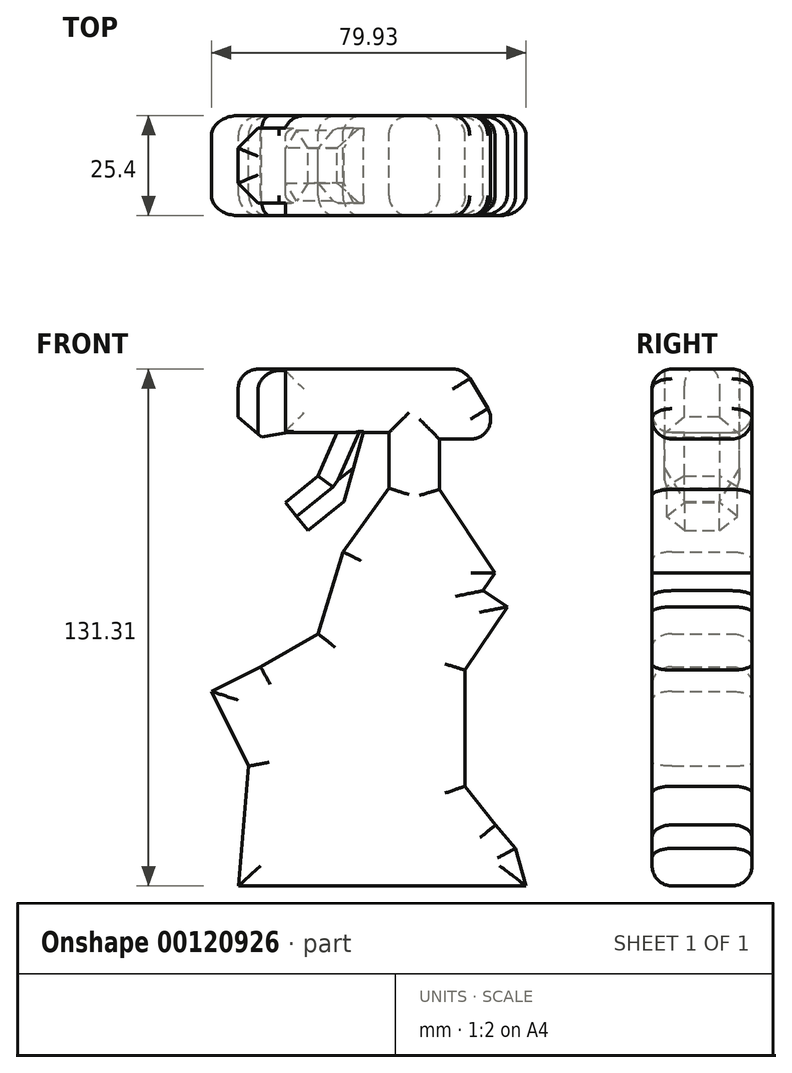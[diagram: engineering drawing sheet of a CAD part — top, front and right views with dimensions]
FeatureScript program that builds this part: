
annotation { "Feature Type Name" : "Feature", "Feature Type Description" : "" }
export const myFeature = defineFeature(function(context is Context, id is Id, definition is map)
    precondition{}
    {
        {
            var Q0;
            Q0=qCreatedBy(makeId("Front.planeOp"),FACE);
            var sketch = newSketch(context, id + "F0", { "sketchPlane" : qUnion([Q0])});
            skLineSegment(sketch, "E0", {"start": v(-38.14, -37.7) * mm, "end": v(34.86, -37.7) * mm});
            skLineSegment(sketch, "E1", {"start": v(34.86, -37.7) * mm, "end": v(32.18, -28.16) * mm});
            skLineSegment(sketch, "E2", {"start": v(32.18, -28.16) * mm, "end": v(27.12, -22.2) * mm});
            skLineSegment(sketch, "E3", {"start": v(27.12, -22.2) * mm, "end": v(19.37, -12.37) * mm});
            skLineSegment(sketch, "E4", {"start": v(19.37, -12.37) * mm, "end": v(19.37, 17.13) * mm});
            skLineSegment(sketch, "E5", {"start": v(19.37, 17.13) * mm, "end": v(30.1, 33.23) * mm});
            skLineSegment(sketch, "E6", {"start": v(30.1, 33.23) * mm, "end": v(23.98, 37.3) * mm});
            skLineSegment(sketch, "E7", {"start": v(23.98, 37.3) * mm, "end": v(26.96, 41.78) * mm});
            skLineSegment(sketch, "E8", {"start": v(26.96, 41.78) * mm, "end": v(12.81, 63.02) * mm});
            skLineSegment(sketch, "E9", {"start": v(12.81, 63.02) * mm, "end": v(12.81, 75.84) * mm});
            skLineSegment(sketch, "E10", {"start": v(12.81, 75.84) * mm, "end": v(29.8, 75.84) * mm});
            skLineSegment(sketch, "E11", {"start": v(29.8, 75.84) * mm, "end": v(19.07, 93.6) * mm});
            skLineSegment(sketch, "E12", {"start": v(19.07, 93.6) * mm, "end": v(-15.87, 93.6) * mm});
            skLineSegment(sketch, "E13", {"start": v(-15.87, 93.6) * mm, "end": v(-26.3, 93.6) * mm});
            skLineSegment(sketch, "E14", {"start": v(-26.3, 93.6) * mm, "end": v(-26.3, 77.44) * mm});
            skLineSegment(sketch, "E15", {"start": v(-26.3, 77.44) * mm, "end": v(0, 77.44) * mm});
            skLineSegment(sketch, "E16", {"start": v(0, 77.44) * mm, "end": v(0, 63.36) * mm});
            skLineSegment(sketch, "E17", {"start": v(0, 63.36) * mm, "end": v(-11.7, 47.2) * mm});
            skLineSegment(sketch, "E18", {"start": v(-11.7, 47.2) * mm, "end": v(-17.95, 26.33) * mm});
            skLineSegment(sketch, "E19", {"start": v(-17.95, 26.33) * mm, "end": v(-32.56, 18) * mm});
            skLineSegment(sketch, "E20", {"start": v(-32.56, 18) * mm, "end": v(-45.07, 11.73) * mm});
            skLineSegment(sketch, "E21", {"start": v(-45.07, 11.73) * mm, "end": v(-35.58, -7.25) * mm});
            skLineSegment(sketch, "E22", {"start": v(-35.58, -7.25) * mm, "end": v(-38.14, -37.7) * mm});
            skLineSegment(sketch, "E23", {"start": v(-26.3, 93.6) * mm, "end": v(-38.3, 93.6) * mm});
            skLineSegment(sketch, "E24", {"start": v(-38.3, 93.6) * mm, "end": v(-38.3, 75.35) * mm});
            skLineSegment(sketch, "E25", {"start": v(-38.3, 75.35) * mm, "end": v(-26.3, 77.44) * mm});
            skLineSegment(sketch, "E26", {"start": v(-13.15, 77.44) * mm, "end": v(-17.95, 66.49) * mm});
            skLineSegment(sketch, "E27", {"start": v(-17.95, 66.49) * mm, "end": v(-26.3, 59.7) * mm});
            skLineSegment(sketch, "E28", {"start": v(-26.3, 59.7) * mm, "end": v(-20.54, 52.62) * mm});
            skLineSegment(sketch, "E29", {"start": v(-20.54, 52.62) * mm, "end": v(-11.43, 60.02) * mm});
            skLineSegment(sketch, "E30", {"start": v(-11.43, 60.02) * mm, "end": v(-6.48, 77.44) * mm});
            skSolve(sketch);
        }
        {
            var Q0;
            Q0=makeQuery(id+"F0.imprint","IMPRINT",FACE,{"disambiguationData":[TD([[makeQuery(id+"F0.imprint","IMPRINT",EDGE,{"derivedFrom":sQuery(id+"F0.wireOp",EDGE,"E0")}),1.0]])]});
            extrude(context, id + "F1", {"entities" : qUnion([Q0]), "endBound" : BoundingType.SYMMETRIC, "depth" : 25.4 * mm});
        }
        {
            var Q0;
            Q0=makeQuery(id+"F0.imprint","IMPRINT",FACE,{"disambiguationData":[TD([[makeQuery(id+"F0.imprint","IMPRINT",EDGE,{"derivedFrom":sQuery(id+"F0.wireOp",EDGE,"E14")}),-1.0]])]});
            var Q1;
            {var subQ0=sQuery(id+"F0.wireOp",EDGE,"E26");Q1=makeQuery(id+"F0.imprint","IMPRINT",FACE,{"disambiguationData":[TD([[makeQuery(id+"F0.imprint","IMPRINT",EDGE,{"derivedFrom":subQ0}),1.0]])]});}
            extrude(context, id + "F2", {"entities" : qUnion([Q0, Q1]), "operationType" : NewBodyOperationType.ADD, "endBound" : BoundingType.SYMMETRIC, "depth" : 19.05 * mm});
        }
        {
            var Q0;
            Q0=makeQuery(id+"F1.opExtrude","CAP_EDGE",EDGE,{"disambiguationData":[OSD([sQuery(id+"F0.wireOp",EDGE,"E22")])],"isStart":false});
            var Q1;
            Q1=makeQuery(id+"F1.opExtrude","CAP_EDGE",EDGE,{"disambiguationData":[OSD([sQuery(id+"F0.wireOp",EDGE,"E21")])],"isStart":false});
            var Q2;
            Q2=makeQuery(id+"F1.opExtrude","CAP_EDGE",EDGE,{"disambiguationData":[OSD([sQuery(id+"F0.wireOp",EDGE,"E0")])],"isStart":false});
            var Q3;
            Q3=makeQuery(id+"F1.opExtrude","CAP_EDGE",EDGE,{"disambiguationData":[OSD([sQuery(id+"F0.wireOp",EDGE,"E1")])],"isStart":false});
            var Q4;
            Q4=makeQuery(id+"F1.opExtrude","CAP_EDGE",EDGE,{"disambiguationData":[OSD([sQuery(id+"F0.wireOp",EDGE,"E20")])],"isStart":false});
            var Q5;
            Q5=makeQuery(id+"F1.opExtrude","CAP_EDGE",EDGE,{"disambiguationData":[OSD([sQuery(id+"F0.wireOp",EDGE,"E18")])],"isStart":false});
            var Q6;
            Q6=makeQuery(id+"F1.opExtrude","CAP_EDGE",EDGE,{"disambiguationData":[OSD([sQuery(id+"F0.wireOp",EDGE,"E17")])],"isStart":false});
            var Q7;
            Q7=makeQuery(id+"F1.opExtrude","CAP_EDGE",EDGE,{"disambiguationData":[OSD([sQuery(id+"F0.wireOp",EDGE,"E16")])],"isStart":false});
            var Q8;
            Q8=makeQuery(id+"F1.opExtrude","CAP_EDGE",EDGE,{"disambiguationData":[OSD([sQuery(id+"F0.wireOp",EDGE,"E15")])],"isStart":false});
            var Q9;
            Q9=makeQuery(id+"F1.opExtrude","CAP_EDGE",EDGE,{"disambiguationData":[OSD([sQuery(id+"F0.wireOp",EDGE,"E12"),sQuery(id+"F0.wireOp",EDGE,"E13")])],"isStart":false});
            var Q10;
            Q10=makeQuery(id+"F1.opExtrude","CAP_EDGE",EDGE,{"disambiguationData":[OSD([sQuery(id+"F0.wireOp",EDGE,"E11")])],"isStart":false});
            var Q11;
            Q11=makeQuery(id+"F1.opExtrude","CAP_EDGE",EDGE,{"disambiguationData":[OSD([sQuery(id+"F0.wireOp",EDGE,"E10")])],"isStart":false});
            var Q12;
            Q12=makeQuery(id+"F1.opExtrude","CAP_EDGE",EDGE,{"disambiguationData":[OSD([sQuery(id+"F0.wireOp",EDGE,"E9")])],"isStart":false});
            var Q13;
            Q13=makeQuery(id+"F1.opExtrude","CAP_EDGE",EDGE,{"disambiguationData":[OSD([sQuery(id+"F0.wireOp",EDGE,"E8")])],"isStart":false});
            var Q14;
            Q14=makeQuery(id+"F1.opExtrude","CAP_EDGE",EDGE,{"disambiguationData":[OSD([sQuery(id+"F0.wireOp",EDGE,"E7")])],"isStart":false});
            var Q15;
            Q15=makeQuery(id+"F1.opExtrude","CAP_EDGE",EDGE,{"disambiguationData":[OSD([sQuery(id+"F0.wireOp",EDGE,"E6")])],"isStart":false});
            var Q16;
            Q16=makeQuery(id+"F1.opExtrude","CAP_EDGE",EDGE,{"disambiguationData":[OSD([sQuery(id+"F0.wireOp",EDGE,"E5")])],"isStart":false});
            var Q17;
            Q17=makeQuery(id+"F1.opExtrude","CAP_EDGE",EDGE,{"disambiguationData":[OSD([sQuery(id+"F0.wireOp",EDGE,"E4")])],"isStart":false});
            var Q18;
            Q18=makeQuery(id+"F1.opExtrude","CAP_EDGE",EDGE,{"disambiguationData":[OSD([sQuery(id+"F0.wireOp",EDGE,"E3")])],"isStart":false});
            var Q19;
            Q19=makeQuery(id+"F1.opExtrude","CAP_EDGE",EDGE,{"disambiguationData":[OSD([sQuery(id+"F0.wireOp",EDGE,"E2")])],"isStart":false});
            var Q20;
            Q20=makeQuery(id+"F1.opExtrude","CAP_EDGE",EDGE,{"disambiguationData":[OSD([sQuery(id+"F0.wireOp",EDGE,"E11")])],"isStart":true});
            var Q21;
            Q21=makeQuery(id+"F1.opExtrude","CAP_EDGE",EDGE,{"disambiguationData":[OSD([sQuery(id+"F0.wireOp",EDGE,"E12"),sQuery(id+"F0.wireOp",EDGE,"E13")])],"isStart":true});
            var Q22;
            Q22=makeQuery(id+"F1.opExtrude","CAP_EDGE",EDGE,{"disambiguationData":[OSD([sQuery(id+"F0.wireOp",EDGE,"E14")])],"isStart":true});
            var Q23;
            Q23=makeQuery(id+"F1.opExtrude","CAP_EDGE",EDGE,{"disambiguationData":[OSD([sQuery(id+"F0.wireOp",EDGE,"E19")])],"isStart":false});
            fillet(context, id + "F3", {"entities" : qUnion([Q0, Q1, Q2, Q3, Q4, Q5, Q6, Q7, Q8, Q9, Q10, Q11, Q12, Q13, Q14, Q15, Q16, Q17, Q18, Q19, Q20, Q21, Q22, Q23]), "radius" : 5.08 * mm, "tangentPropagation" : true, "allowEdgeOverflow" : false});
        }
        {
            var Q0;
            Q0=makeQuery(id+"F1.opExtrude","CAP_EDGE",EDGE,{"disambiguationData":[OSD([sQuery(id+"F0.wireOp",EDGE,"E9")])],"isStart":true});
            var Q1;
            Q1=makeQuery(id+"F1.opExtrude","CAP_EDGE",EDGE,{"disambiguationData":[OSD([sQuery(id+"F0.wireOp",EDGE,"E10")])],"isStart":true});
            var Q2;
            Q2=makeQuery(id+"F1.opExtrude","CAP_EDGE",EDGE,{"disambiguationData":[OSD([sQuery(id+"F0.wireOp",EDGE,"E8")])],"isStart":true});
            var Q3;
            Q3=makeQuery(id+"F1.opExtrude","CAP_EDGE",EDGE,{"disambiguationData":[OSD([sQuery(id+"F0.wireOp",EDGE,"E7")])],"isStart":true});
            var Q4;
            Q4=makeQuery(id+"F1.opExtrude","CAP_EDGE",EDGE,{"disambiguationData":[OSD([sQuery(id+"F0.wireOp",EDGE,"E6")])],"isStart":true});
            var Q5;
            Q5=makeQuery(id+"F1.opExtrude","CAP_EDGE",EDGE,{"disambiguationData":[OSD([sQuery(id+"F0.wireOp",EDGE,"E4")])],"isStart":true});
            var Q6;
            Q6=makeQuery(id+"F1.opExtrude","CAP_EDGE",EDGE,{"disambiguationData":[OSD([sQuery(id+"F0.wireOp",EDGE,"E5")])],"isStart":true});
            var Q7;
            Q7=makeQuery(id+"F1.opExtrude","CAP_EDGE",EDGE,{"disambiguationData":[OSD([sQuery(id+"F0.wireOp",EDGE,"E3")])],"isStart":true});
            var Q8;
            Q8=makeQuery(id+"F1.opExtrude","CAP_EDGE",EDGE,{"disambiguationData":[OSD([sQuery(id+"F0.wireOp",EDGE,"E2")])],"isStart":true});
            var Q9;
            Q9=makeQuery(id+"F1.opExtrude","CAP_EDGE",EDGE,{"disambiguationData":[OSD([sQuery(id+"F0.wireOp",EDGE,"E0")])],"isStart":true});
            var Q10;
            Q10=makeQuery(id+"F1.opExtrude","CAP_EDGE",EDGE,{"disambiguationData":[OSD([sQuery(id+"F0.wireOp",EDGE,"E22")])],"isStart":true});
            var Q11;
            Q11=makeQuery(id+"F1.opExtrude","CAP_EDGE",EDGE,{"disambiguationData":[OSD([sQuery(id+"F0.wireOp",EDGE,"E1")])],"isStart":true});
            var Q12;
            Q12=makeQuery(id+"F1.opExtrude","CAP_EDGE",EDGE,{"disambiguationData":[OSD([sQuery(id+"F0.wireOp",EDGE,"E21")])],"isStart":true});
            var Q13;
            Q13=makeQuery(id+"F1.opExtrude","CAP_EDGE",EDGE,{"disambiguationData":[OSD([sQuery(id+"F0.wireOp",EDGE,"E20")])],"isStart":true});
            var Q14;
            Q14=makeQuery(id+"F1.opExtrude","CAP_EDGE",EDGE,{"disambiguationData":[OSD([sQuery(id+"F0.wireOp",EDGE,"E19")])],"isStart":true});
            var Q15;
            Q15=makeQuery(id+"F1.opExtrude","CAP_EDGE",EDGE,{"disambiguationData":[OSD([sQuery(id+"F0.wireOp",EDGE,"E18")])],"isStart":true});
            var Q16;
            Q16=makeQuery(id+"F1.opExtrude","CAP_EDGE",EDGE,{"disambiguationData":[OSD([sQuery(id+"F0.wireOp",EDGE,"E17")])],"isStart":true});
            var Q17;
            Q17=makeQuery(id+"F1.opExtrude","CAP_EDGE",EDGE,{"disambiguationData":[OSD([sQuery(id+"F0.wireOp",EDGE,"E16")])],"isStart":true});
            var Q18;
            Q18=makeQuery(id+"F1.opExtrude","CAP_EDGE",EDGE,{"disambiguationData":[OSD([sQuery(id+"F0.wireOp",EDGE,"E15")])],"isStart":true});
            fillet(context, id + "F4", {"entities" : qUnion([Q0, Q1, Q2, Q3, Q4, Q5, Q6, Q7, Q8, Q9, Q10, Q11, Q12, Q13, Q14, Q15, Q16, Q17, Q18]), "radius" : 5.08 * mm, "tangentPropagation" : true, "allowEdgeOverflow" : false});
        }
        {
            var Q0;
            Q0=makeQuery(id+"F2.opExtrude","CAP_EDGE",EDGE,{"disambiguationData":[OSD([sQuery(id+"F0.wireOp",EDGE,"E27")])],"isStart":true});
            var Q1;
            Q1=makeQuery(id+"F2.opExtrude","CAP_EDGE",EDGE,{"disambiguationData":[OSD([sQuery(id+"F0.wireOp",EDGE,"E26")])],"isStart":true});
            var Q2;
            Q2=makeQuery(id+"F2.opExtrude","CAP_EDGE",EDGE,{"disambiguationData":[OSD([sQuery(id+"F0.wireOp",EDGE,"E27")])],"isStart":false});
            var Q3;
            Q3=makeQuery(id+"F2.opExtrude","CAP_EDGE",EDGE,{"disambiguationData":[OSD([sQuery(id+"F0.wireOp",EDGE,"E26")])],"isStart":false});
            var Q4;
            Q4=makeQuery(id+"F2.opExtrude","CAP_EDGE",EDGE,{"disambiguationData":[OSD([sQuery(id+"F0.wireOp",EDGE,"E29")])],"isStart":false});
            var Q5;
            Q5=makeQuery(id+"F2.opExtrude","CAP_EDGE",EDGE,{"disambiguationData":[OSD([sQuery(id+"F0.wireOp",EDGE,"E29")])],"isStart":true});
            var Q6;
            Q6=makeQuery(id+"F2.opExtrude","CAP_EDGE",EDGE,{"disambiguationData":[OSD([sQuery(id+"F0.wireOp",EDGE,"E24")])],"isStart":true});
            var Q7;
            Q7=makeQuery(id+"F2.opExtrude","CAP_EDGE",EDGE,{"disambiguationData":[OSD([sQuery(id+"F0.wireOp",EDGE,"E24")])],"isStart":false});
            var Q8;
            Q8=makeQuery(id+"F2.opExtrude","SWEPT_EDGE",EDGE,{"disambiguationData":[OSD([sQuery(id+"F0.wireOp",EDGE,"E24"),sQuery(id+"F0.wireOp",EDGE,"E25")])]});
            chamfer(context, id + "F5", {"entities" : qUnion([Q0, Q1, Q2, Q3, Q4, Q5, Q6, Q7, Q8]), "width" : 5.08 * mm, "tangentPropagation" : true});
        }
        {
            var Q0;
            Q0=makeQuery(id+"F2.boolean.opBoolean","MERGE",FACE,{"derivedFrom":[makeQuery(id+"F1.opExtrude","SWEPT_FACE",FACE,{"disambiguationData":[OSD([sQuery(id+"F0.wireOp",EDGE,"E12"),sQuery(id+"F0.wireOp",EDGE,"E13")])]}),makeQuery(id+"F2.opExtrude","SWEPT_FACE",FACE,{"disambiguationData":[OSD([sQuery(id+"F0.wireOp",EDGE,"E23")])]})]});
            fillet(context, id + "F6", {"entities" : qUnion([Q0]), "radius" : 5.08 * mm, "tangentPropagation" : true, "allowEdgeOverflow" : false});
        }
    });
